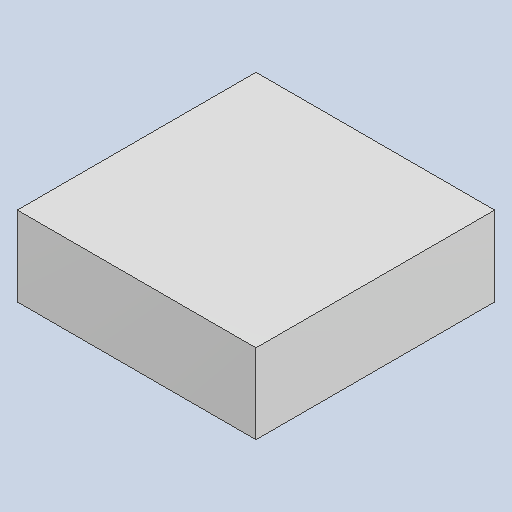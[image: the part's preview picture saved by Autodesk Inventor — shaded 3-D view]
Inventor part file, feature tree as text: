
AUTODESK INVENTOR PART (.ipt)
format: ipt  version: 2023.4 (Build 274418000, 418)  size: 79,872 bytes
history: native  units: mm
features: extrude x1
ambient origin geometry x8: Origin, YZ Plane, XZ Plane, XY Plane, X Axis, Y Axis, Z Axis, Center Point
bodies: Solid1 (feature_tree)
feature tree (1):
  extrude  "Extruded_55"  [1 undecoded]
note: 1 required parameter value undecoded (feature->parameter linkage not recoverable at this tier; creation-order binding heuristic only, values carry confidence <= 0.55)
